# Revit family: VLN_Nim-II-Mes-E_Multiproduct_BIM_NL_F3050;F3051
name_source: partatom
category: Plumbing Fixtures
revit_build: Autodesk Revit MEP 2014 (Build: 20130308_1515(x64)
units: mm (PartAtom-declared; Revit-internal decimal feet)

## types (2) — shared parameters
Accessories = www.idealstandardnederland.nl
AreaUnits = millimeters
Assembly Code = C1030200
AssetType = Vast
BREEAMApproved = No
Brand = Venlo
CodePerformance = EN 817, DIN 4109
Color = Chroom
ConnectionType = Sanitair
Default Elevation = 800 mm  [stored 2.62467 ft]
DurationUnit = jaar
ECA = No
ExpectedLife = 25
FaucetFunction = Mengkraan
FaucetOperation = Tweegreeps
FaucetType = Wastafelmengkraan
Finish = Chroom
IfcExportAs = IfcValveType
IfcExportType = FAUCET
InstallationInstructions = http://www.idealstandardnederland.nl
LinearUnits = millimeters
ManufacturerURL = www.idealstandardnederland.nl
Material = Messing
NBSDescription = Water supply fittings for wash basins and troughs
NBSReference = 45-35-70/371
NettWeight = 1.228 kg
NominalHeight = 236 mm
NominalLength = 158 mm
NominalWidth = 143 mm
ProductInformation = http://www.idealstandardnederland.nl
Shape = Gesculptuurd
Size = 143 x 158 x236 mm
Space = Internal
SpareParts = www.idealstandardnederland.nl
TMV3 = Yes
TestPressure = 10 Bar
URL = www.idealstandardnederland.nl
Uniclass2015Code = Pr_40_20_87_98
Uniclass2015Title = Washbasin taps
Uniclass2015Version = Products v1.1
ValveMechanism = Keramische schijven
ValveOperation = Tweegreeps
Version = 1
VolumeUnits = liter
WRAS = No
WarrantyDescription = Fabrieksgarantie
WarrantyDurationParts = 10
WarrantyDurationUnit = jaar
WaterEfficientProduct = No
WorkingPressure = 1-5 bar
zero-valued in all types: CWFU, Cost, HWFU, WFU

## per-type parameters (varying)
| type | BIMObjectName | BarCode | Description | Features | FlowRate | Model | ModelNumber | ModelReference | Name |
| F3050AA - NIM-II-MES-E WASTAFEL M KR 1-G 5L/MIN | VLN_Venlo_WashbasinTaps_F3050AA | 8711678064714 | Venlo Nimbus II Messing wastafelmengkraan 5 l/min eco. Eengats. Draaibare uitloop. Straalregelaar. Ketting. Sprong 135 mm. Hoogte uitloop 150 mm. Bovenbevestiging (TOP FIX). Eco bovendelen. | Wastafelmengkraan 5 l/min eco. Eengats. Draaibare uitloop. Straalregelaar. Ketting. Sprong 135 mm. Hoogte uitloop 150 mm. Bovenbevestiging (TOP FIX). Eco bovendelen. | 5 liter @ 3 bar | F3050AA | F3050AA | Venlo Nimbus II Messing wastafelmengkraan 5 l/min eco. Eengats. Draaibare uitloop. Straalregelaar. Ketting. Sprong 135 mm. Hoogte uitloop 150 mm. Bovenbevestiging (TOP FIX). Eco bovendelen. | WashbasinTaps_F3050AA_Venlo |
| F3051AA - NIM-II-MES-E WASTAFEL M KR 1-G CHR | VLN_Venlo_WashbasinTaps_F3051AA | 8711678062895 | Venlo Nimbus II Messing wastafelmengkraan eco. Eengats. Draaibare uitloop. Straalregelaar. Ketting. Sprong 135 mm. Hoogte uitloop 150 mm. Bovenbevestiging (TOP FIX). Eco bovendelen. | Wastafelmengkraan eco. Eengats. Draaibare uitloop. Straalregelaar. Ketting. Sprong 135 mm. Hoogte uitloop 150 mm. Bovenbevestiging (TOP FIX). Eco bovendelen. | 7,5 liter @ 3 bar | F3051AA | F3051AA | Venlo Nimbus II Messing wastafelmengkraan eco. Eengats. Draaibare uitloop. Straalregelaar. Ketting. Sprong 135 mm. Hoogte uitloop 150 mm. Bovenbevestiging (TOP FIX). Eco bovendelen. | WashbasinTaps_F3051AA_Venlo |

note: [stored X ft] marks values corroborated as IEEE doubles in the binary element streams (Revit-internal decimal feet)

## geometry (parser evidence)
native form markers: Sweep x1
no freeform markers — native parametric forms only
